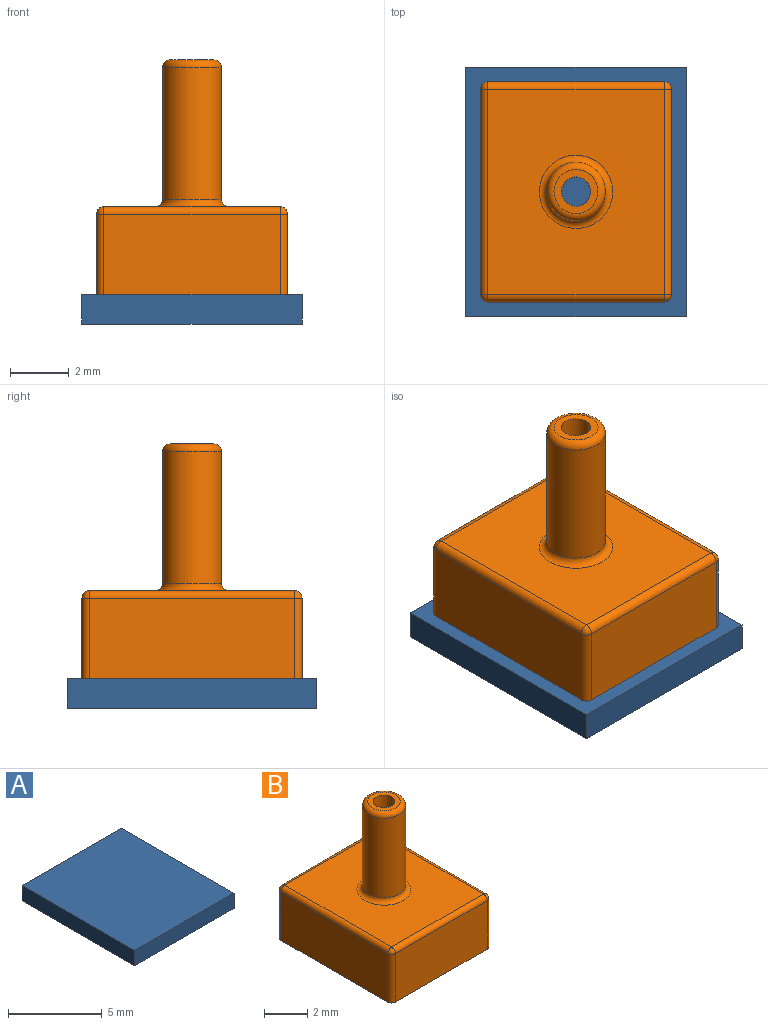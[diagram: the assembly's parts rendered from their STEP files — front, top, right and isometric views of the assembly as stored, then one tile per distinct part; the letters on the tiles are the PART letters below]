
ASSEMBLY  parts=2 mates=1
PART A: 6 faces, bbox 7.5x8.5x1 mm
  f0: plane 7.5x1mm, normal (0,-1,0), area 7.5mm2, adj f1,f3,f4,f5
  f1: plane 8.5x1mm, normal (1,0,0), area 8.5mm2, adj f0,f2,f4,f5
  f2: plane 7.5x1mm, normal (0,1,0), area 7.5mm2, adj f1,f3,f4,f5
  f3: plane 8.5x1mm, normal (-1,0,0), area 8.5mm2, adj f0,f2,f4,f5
  f4: plane 8.5x7.5mm, normal (0,0,1), area 63.7mm2, adj f0,f1,f2,f3
  f5: plane 8.5x7.5mm, normal (0,0,-1), area 63.7mm2, adj f0,f1,f2,f3
PART B: 29 faces, bbox 6.5x7.5x8 mm
  f0: plane 6x2.75mm, normal (0,-1,0), area 16.5mm2, adj f5,f19,f25,f28
  f1: plane 7x2.75mm, normal (1,0,0), area 19.2mm2, adj f5,f22,f26,f28
  f2: plane 6x2.75mm, normal (0,1,0), area 16.5mm2, adj f5,f17,f21,f22
  f3: plane 7x2.75mm, normal (-1,0,0), area 19.2mm2, adj f5,f17,f19,f20
  f4: plane 7x6mm, normal (0,0,1), area 37.1mm2, adj f15,f20,f21,f25,f26
  f5: plane 7.5x6.5mm, normal (0,0,-1), area 18.7mm2, adj f0,f1,f2,f3,f8,f9,f10,f11
  f6: cylinder r=1mm len=4.5mm, axis (0,0,-1), area 28.3mm2, adj f15,f16
  f7: plane 1.5x1.5mm, normal (0,0,1), area 1mm2, adj f13,f16
  f8: plane 6x2.25mm, normal (1,0,0), area 13.5mm2, adj f5,f9,f11,f12
  f9: plane 5x2.25mm, normal (0,-1,0), area 11.2mm2, adj f5,f8,f10,f12
  f10: plane 6x2.25mm, normal (-1,0,0), area 13.5mm2, adj f5,f9,f11,f12
  f11: plane 5x2.25mm, normal (0,1,0), area 11.2mm2, adj f5,f8,f10,f12
  f12: plane 6x5mm, normal (0,0,-1), area 28.2mm2, adj f8,f9,f10,f11,f14
  f13: cylinder r=0.5mm len=5.5mm, axis (0,0,1), area 17.3mm2, adj f7,f14
  f14: torus R=0.75mm, axis (0,0,-1), area 1.5mm2, adj f12,f13
  f15: torus R=1.25mm, axis (0,0,1), area 2.7mm2, adj f4,f6
  f16: torus R=0.75mm, axis (0,0,1), area 2.2mm2, adj f6,f7
  f17: cylinder r=0.25mm len=2.75mm, axis (0,0,1), area 1.1mm2, adj f2,f3,f5,f18
  f18: sphere r=0.25mm, area 0.1mm2, adj f17,f20,f21
  f19: cylinder r=0.25mm len=2.75mm, axis (0,0,-1), area 1.1mm2, adj f0,f3,f5,f23
  f20: cylinder r=0.25mm len=7mm, axis (0,1,0), area 2.7mm2, adj f3,f4,f18,f23
  f21: cylinder r=0.25mm len=6mm, axis (1,0,0), area 2.4mm2, adj f2,f4,f18,f24
  f22: cylinder r=0.25mm len=2.75mm, axis (0,0,-1), area 1.1mm2, adj f1,f2,f5,f24
  f23: sphere r=0.25mm, area 0.1mm2, adj f19,f20,f25
  f24: sphere r=0.25mm, area 0.1mm2, adj f21,f22,f26
  f25: cylinder r=0.25mm len=6mm, axis (-1,0,0), area 2.4mm2, adj f0,f4,f23,f27
  f26: cylinder r=0.25mm len=7mm, axis (0,-1,0), area 2.7mm2, adj f1,f4,f24,f27
  f27: sphere r=0.25mm, area 0.1mm2, adj f25,f26,f28
  f28: cylinder r=0.25mm len=2.75mm, axis (0,0,1), area 1.1mm2, adj f0,f1,f5,f27
PLACE A rot(axis=(1,0,0),180deg) t=(0,0,0)mm fixed
PLACE B rot(axis=(0,0,1),180deg) t=(0,0,0)mm
MATE cylindrical B.f6 <-> A.f5  axis (0,0,-1) through (0,0,0)mm
